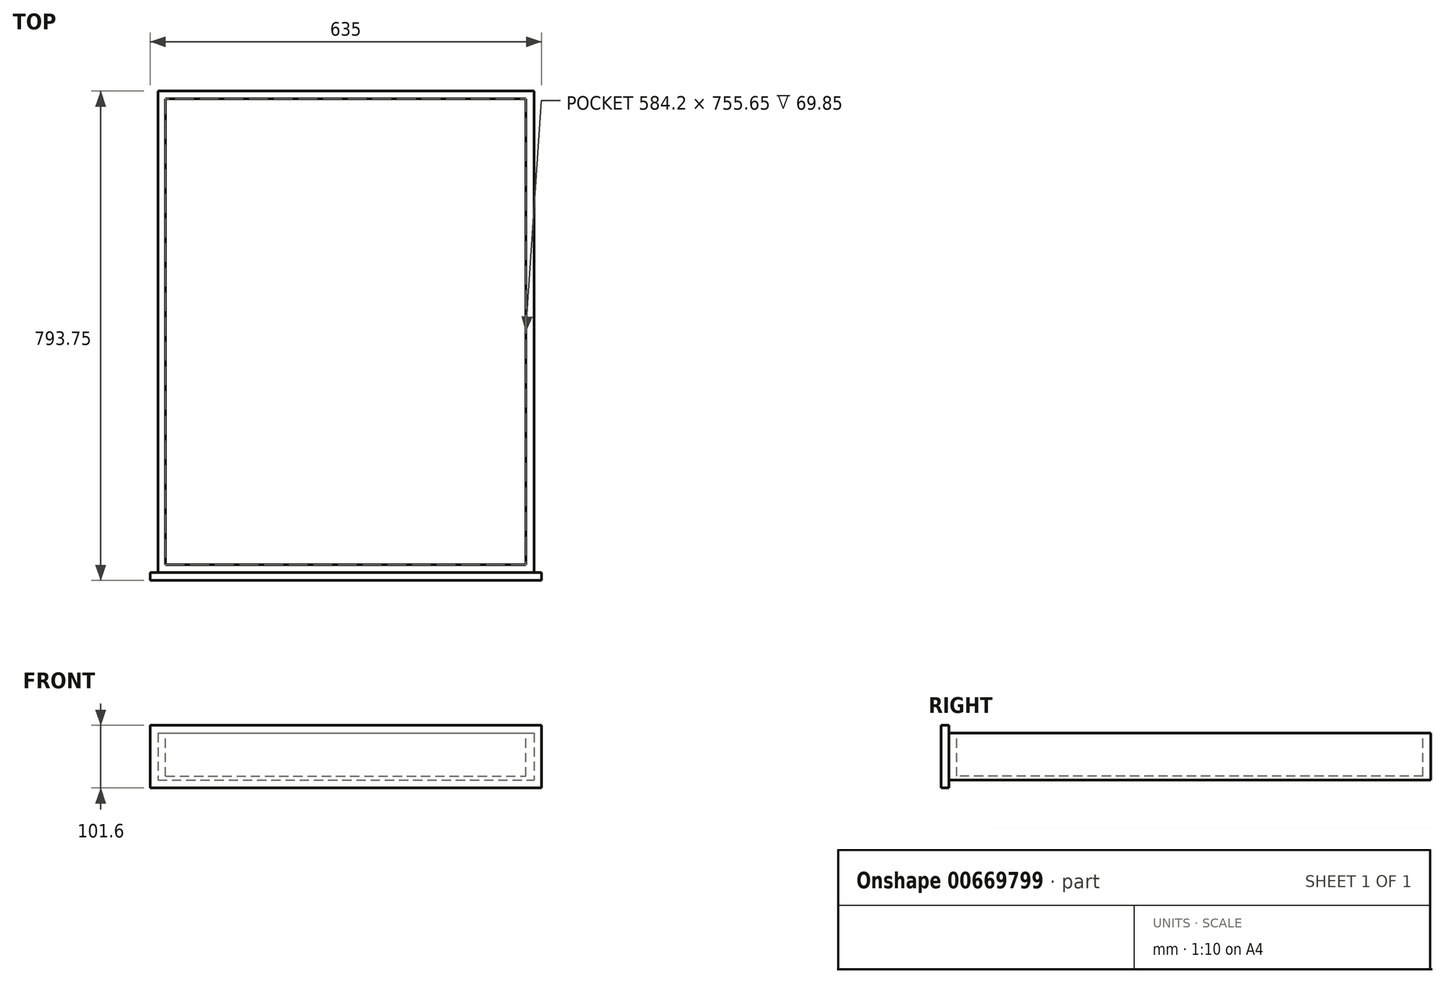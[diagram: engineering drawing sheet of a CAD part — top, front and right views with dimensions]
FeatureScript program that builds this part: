
annotation { "Feature Type Name" : "Feature", "Feature Type Description" : "" }
export const myFeature = defineFeature(function(context is Context, id is Id, definition is map)
    precondition{}
    {
        {
            var Q0;
            Q0=qCreatedBy(makeId("Front.planeOp"),FACE);
            var sketch = newSketch(context, id + "F0", { "sketchPlane" : qUnion([Q0])});
            skLineSegment(sketch, "E0.bottom", {"start": v(-317.5, 50.8) * mm, "end": v(317.5, 50.8) * mm});
            skLineSegment(sketch, "E0.top", {"start": v(-317.5, -50.8) * mm, "end": v(317.5, -50.8) * mm});
            skLineSegment(sketch, "E0.left", {"start": v(-317.5, 50.8) * mm, "end": v(-317.5, -50.8) * mm});
            skLineSegment(sketch, "E0.right", {"start": v(317.5, 50.8) * mm, "end": v(317.5, -50.8) * mm});
            skPoint(sketch, "E0.middle", {"position": v(0, 0) * mm});
            skLineSegment(sketch, "E1.bottom", {"start": v(-304.8, 38.1) * mm, "end": v(304.8, 38.1) * mm});
            skLineSegment(sketch, "E1.top", {"start": v(-304.8, -38.1) * mm, "end": v(304.8, -38.1) * mm});
            skLineSegment(sketch, "E1.left", {"start": v(-304.8, 38.1) * mm, "end": v(-304.8, -38.1) * mm});
            skLineSegment(sketch, "E1.right", {"start": v(304.8, 38.1) * mm, "end": v(304.8, -38.1) * mm});
            skSolve(sketch);
        }
        {
            var Q0;
            Q0=makeQuery(id+"F0.imprint","IMPRINT",FACE,{"disambiguationData":[TD([[makeQuery(id+"F0.imprint","IMPRINT",EDGE,{"derivedFrom":sQuery(id+"F0.wireOp",EDGE,"E0.bottom")}),-1.0]])]});
            var Q1;
            Q1=makeQuery(id+"F0.imprint","IMPRINT",FACE,{"disambiguationData":[TD([[makeQuery(id+"F0.imprint","IMPRINT",EDGE,{"derivedFrom":sQuery(id+"F0.wireOp",EDGE,"E1.bottom")}),-1.0]])]});
            extrude(context, id + "F1", {"entities" : qUnion([Q0, Q1]), "depth" : 12.7 * mm, "offsetDistance" : 25.4 * mm});
        }
        {
            var Q0;
            Q0=makeQuery(id+"F0.imprint","IMPRINT",FACE,{"disambiguationData":[TD([[makeQuery(id+"F0.imprint","IMPRINT",EDGE,{"derivedFrom":sQuery(id+"F0.wireOp",EDGE,"E1.bottom")}),-1.0]])]});
            extrude(context, id + "F2", {"entities" : qUnion([Q0]), "oppositeDirection" : true, "depth" : 781.05 * mm, "offsetDistance" : 25.4 * mm});
        }
        {
            var Q0;
            Q0=makeQuery(id+"F2.opExtrude","SWEPT_FACE",FACE,{"disambiguationData":[OSD([sQuery(id+"F0.wireOp",EDGE,"E1.bottom")])]});
            var sketch = newSketch(context, id + "F3", { "sketchPlane" : qUnion([Q0])});
            skLineSegment(sketch, "E2.0", {"start": v(-292.1, 12.7) * mm, "end": v(292.1, 12.7) * mm});
            skLineSegment(sketch, "E2.1", {"start": v(-292.1, 768.35) * mm, "end": v(-292.1, 12.7) * mm});
            skLineSegment(sketch, "E2.2", {"start": v(292.1, 768.35) * mm, "end": v(-292.1, 768.35) * mm});
            skLineSegment(sketch, "E2.3", {"start": v(292.1, 12.7) * mm, "end": v(292.1, 768.35) * mm});
            skSolve(sketch);
        }
        {
            var Q0;
            Q0=makeQuery(id+"F3.imprint","IMPRINT",FACE,{"disambiguationData":[TD([[makeQuery(id+"F3.imprint","IMPRINT",EDGE,{"derivedFrom":sQuery(id+"F3.wireOp",EDGE,"E2.0")}),1.0]])]});
            extrude(context, id + "F4", {"entities" : qUnion([Q0]), "operationType" : NewBodyOperationType.REMOVE, "oppositeDirection" : true, "depth" : 69.85 * mm, "offsetDistance" : 25.4 * mm});
        }
    });
